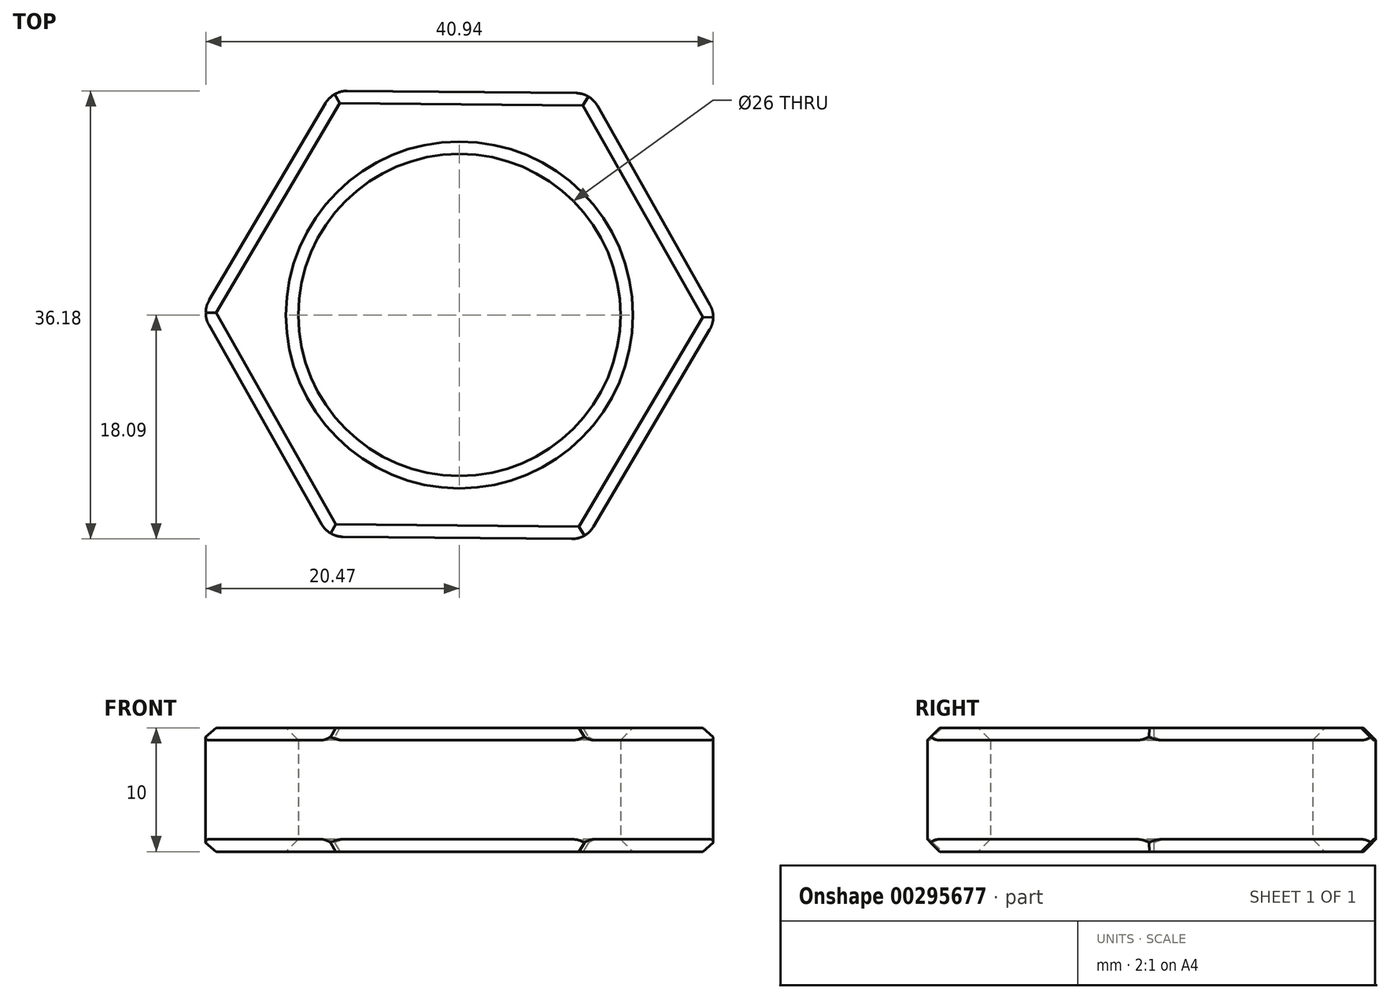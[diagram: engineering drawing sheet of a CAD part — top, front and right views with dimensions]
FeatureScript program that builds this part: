
annotation { "Feature Type Name" : "Feature", "Feature Type Description" : "" }
export const myFeature = defineFeature(function(context is Context, id is Id, definition is map)
    precondition{}
    {
        {
            var Q0;
            Q0=qCreatedBy(makeId("Top.planeOp"),FACE);
            var sketch = newSketch(context, id + "F0", { "sketchPlane" : qUnion([Q0])});
            skCircle(sketch, "E0.cCircle", {"center": v(0, 0) * mm, "radius": 20.78 * mm, "construction": true});
            skLineSegment(sketch, "E0.0", {"start": v(10.22, -18.1) * mm, "end": v(-10.56, -17.9) * mm});
            skLineSegment(sketch, "E0.1", {"start": v(-10.56, -17.9) * mm, "end": v(-20.78, 0.2) * mm});
            skLineSegment(sketch, "E0.2", {"start": v(-20.78, 0.2) * mm, "end": v(-10.22, 18.1) * mm});
            skLineSegment(sketch, "E0.3", {"start": v(-10.22, 18.1) * mm, "end": v(10.56, 17.9) * mm});
            skLineSegment(sketch, "E0.4", {"start": v(10.56, 17.9) * mm, "end": v(20.78, -0.2) * mm});
            skLineSegment(sketch, "E0.5", {"start": v(20.78, -0.2) * mm, "end": v(10.22, -18.1) * mm});
            skCircle(sketch, "E1", {"center": v(0, 0) * mm, "radius": 13 * mm});
            skSolve(sketch);
        }
        {
            var Q0;
            Q0=makeQuery(id+"F0.imprint","IMPRINT",FACE,{"disambiguationData":[TD([[makeQuery(id+"F0.imprint","IMPRINT",EDGE,{"derivedFrom":sQuery(id+"F0.wireOp",EDGE,"E0.0")}),-1.0]])]});
            extrude(context, id + "F1", {"entities" : qUnion([Q0]), "depth" : 10 * mm, "symmetric" : true});
        }
        {
            var Q0;
            Q0=makeQuery(id+"F1.opExtrude","CAP_FACE",FACE,{"disambiguationData":[OSD([sQuery(id+"F0.wireOp",EDGE,"E0.0"),sQuery(id+"F0.wireOp",EDGE,"E0.1"),sQuery(id+"F0.wireOp",EDGE,"E0.2"),sQuery(id+"F0.wireOp",EDGE,"E0.3"),sQuery(id+"F0.wireOp",EDGE,"E0.4"),sQuery(id+"F0.wireOp",EDGE,"E0.5"),sQuery(id+"F0.wireOp",EDGE,"E1")])],"isStart":false});
            var Q1;
            Q1=makeQuery(id+"F1.opExtrude","CAP_FACE",FACE,{"disambiguationData":[OSD([sQuery(id+"F0.wireOp",EDGE,"E0.0"),sQuery(id+"F0.wireOp",EDGE,"E0.1"),sQuery(id+"F0.wireOp",EDGE,"E0.2"),sQuery(id+"F0.wireOp",EDGE,"E0.3"),sQuery(id+"F0.wireOp",EDGE,"E0.4"),sQuery(id+"F0.wireOp",EDGE,"E0.5"),sQuery(id+"F0.wireOp",EDGE,"E1")])],"isStart":true});
            chamfer(context, id + "F2", {"entities" : qUnion([Q0, Q1]), "width" : 1 * mm, "tangentPropagation" : true});
        }
        {
            var Q0;
            Q0=makeQuery(id+"F1.opExtrude","SWEPT_EDGE",EDGE,{"disambiguationData":[OSD([sQuery(id+"F0.wireOp",EDGE,"E0.3"),sQuery(id+"F0.wireOp",EDGE,"E0.4")])]});
            var Q1;
            Q1=makeQuery(id+"F1.opExtrude","SWEPT_EDGE",EDGE,{"disambiguationData":[OSD([sQuery(id+"F0.wireOp",EDGE,"E0.2"),sQuery(id+"F0.wireOp",EDGE,"E0.3")])]});
            var Q2;
            Q2=makeQuery(id+"F1.opExtrude","SWEPT_EDGE",EDGE,{"disambiguationData":[OSD([sQuery(id+"F0.wireOp",EDGE,"E0.1"),sQuery(id+"F0.wireOp",EDGE,"E0.2")])]});
            var Q3;
            Q3=makeQuery(id+"F1.opExtrude","SWEPT_EDGE",EDGE,{"disambiguationData":[OSD([sQuery(id+"F0.wireOp",EDGE,"E0.0"),sQuery(id+"F0.wireOp",EDGE,"E0.1")])]});
            var Q4;
            Q4=makeQuery(id+"F1.opExtrude","SWEPT_EDGE",EDGE,{"disambiguationData":[OSD([sQuery(id+"F0.wireOp",EDGE,"E0.0"),sQuery(id+"F0.wireOp",EDGE,"E0.5")])]});
            var Q5;
            Q5=makeQuery(id+"F1.opExtrude","SWEPT_EDGE",EDGE,{"disambiguationData":[OSD([sQuery(id+"F0.wireOp",EDGE,"E0.4"),sQuery(id+"F0.wireOp",EDGE,"E0.5")])]});
            fillet(context, id + "F3", {"entities" : qUnion([Q0, Q1, Q2, Q3, Q4, Q5]), "radius" : 2 * mm, "tangentPropagation" : true, "allowEdgeOverflow" : false});
        }
    });
